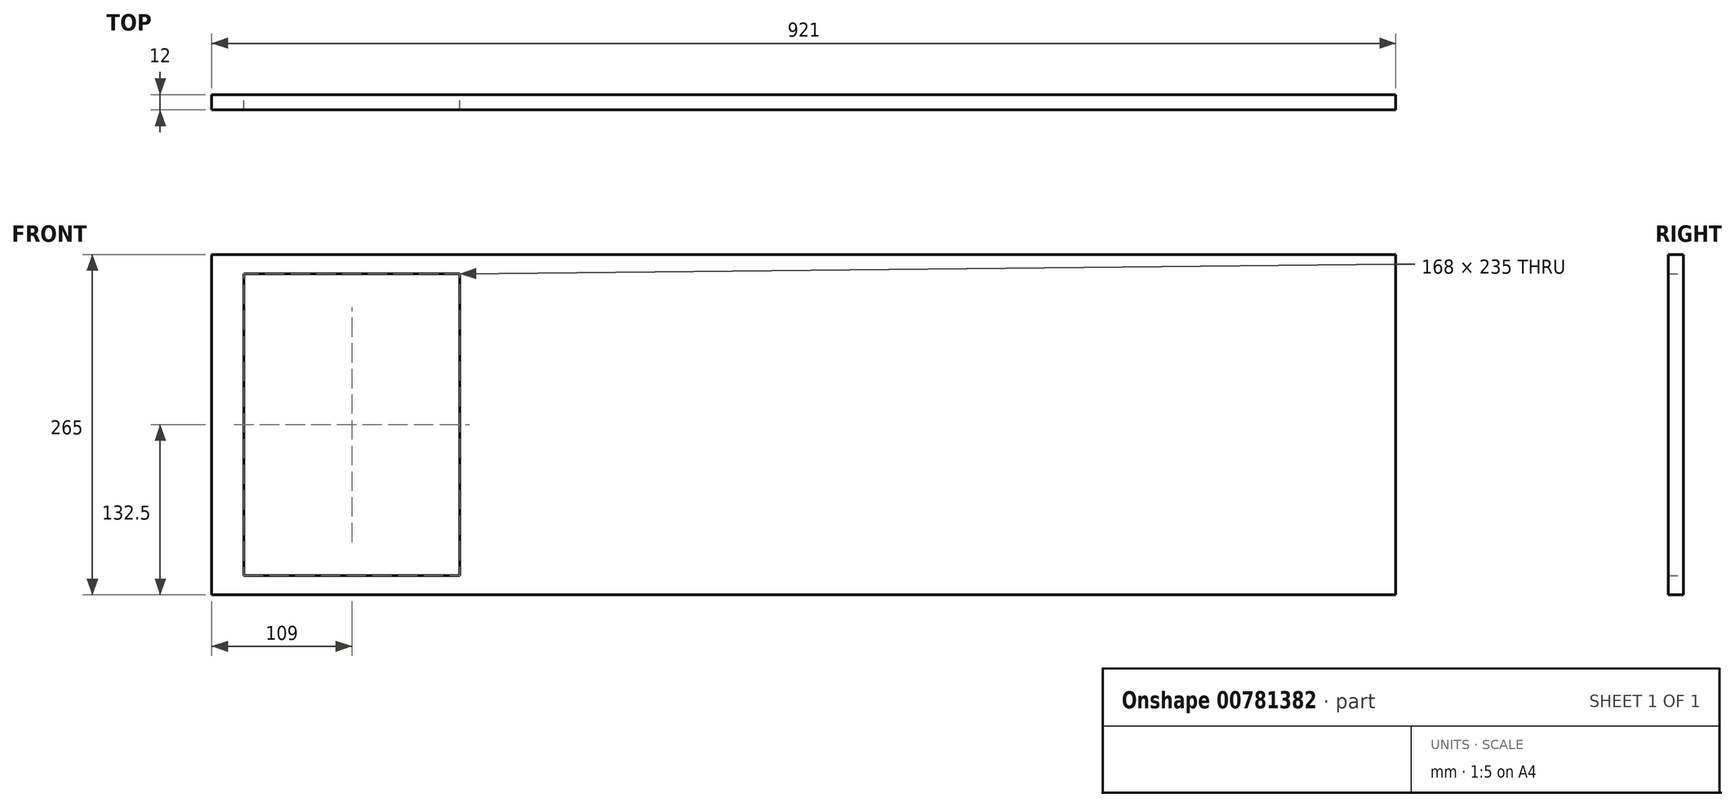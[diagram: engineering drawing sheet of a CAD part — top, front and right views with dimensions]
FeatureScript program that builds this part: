
annotation { "Feature Type Name" : "Feature", "Feature Type Description" : "" }
export const myFeature = defineFeature(function(context is Context, id is Id, definition is map)
    precondition{}
    {
        {
            var Q0;
            Q0=qCreatedBy(makeId("Front.planeOp"),FACE);
            var sketch = newSketch(context, id + "F0", { "sketchPlane" : qUnion([Q0])});
            skLineSegment(sketch, "E0.bottom", {"start": v(-460.5, -132.5) * mm, "end": v(460.5, -132.5) * mm});
            skLineSegment(sketch, "E0.top", {"start": v(-460.5, 132.5) * mm, "end": v(460.5, 132.5) * mm});
            skLineSegment(sketch, "E0.left", {"start": v(-460.5, -132.5) * mm, "end": v(-460.5, 132.5) * mm});
            skLineSegment(sketch, "E0.right", {"start": v(460.5, -132.5) * mm, "end": v(460.5, 132.5) * mm});
            skPoint(sketch, "E0.middle", {"position": v(0, 0) * mm});
            skLineSegment(sketch, "E1.bottom", {"start": v(-267.5, -117.5) * mm, "end": v(-435.5, -117.5) * mm});
            skLineSegment(sketch, "E1.top", {"start": v(-267.5, 117.5) * mm, "end": v(-435.5, 117.5) * mm});
            skLineSegment(sketch, "E1.left", {"start": v(-267.5, -117.5) * mm, "end": v(-267.5, 117.5) * mm});
            skLineSegment(sketch, "E1.right", {"start": v(-435.5, -117.5) * mm, "end": v(-435.5, 117.5) * mm});
            skPoint(sketch, "E1.middle", {"position": v(-351.5, 0) * mm});
            skSolve(sketch);
        }
        {
            var Q0;
            Q0 = qSketchRegion(id + "F0", true);
            extrude(context, id + "F1", {"entities" : qUnion([Q0]), "depth" : 12 * mm, "offsetDistance" : 25 * mm});
        }
    });
